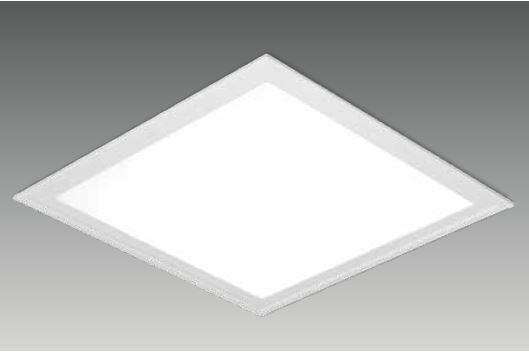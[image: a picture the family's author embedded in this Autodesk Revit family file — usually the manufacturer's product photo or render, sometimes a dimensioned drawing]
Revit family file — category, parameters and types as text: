
# Revit family: G 3030 OPL
name_source: partatom
category: Lighting Fixtures
revit_build: Autodesk Revit 2017 (Build: 20160225_1515(x64)
units: mm (PartAtom-declared; Revit-internal decimal feet)

## family parameters
Always vertical = Yes
Cut with Voids When Loaded = No
Host = Ceiling
Light Source = Yes
OmniClass Number = 23.80.70.11
OmniClass Title = Luminaries for Internal Lighting
Part Type = Normal
Room Calculation Point = No
Round Connector Dimension = Use Diameter
Shared = No

## types (2) — shared parameters
Apparent Load = 10 VA
Color Filter = 16777215
Dimming Lamp Color Temperature Shift = <None>
Emit Shape Visible in Rendering = Yes
Emit from Rectangle Length = 320 mm  [stored 1.04987 ft]
Emit from Rectangle Width = 320 mm  [stored 1.04987 ft]
Light Source Symbol Size = 610 mm
Manufacturer = ARLIGHT
Type Image = G 3030 OPL.JPG
Wattage Comments = 10

## type names (no varying parameters)
- GOPL.3030.10.30
- GOPL.3030.10.40

note: [stored X ft] marks values corroborated as IEEE doubles in the binary element streams (Revit-internal decimal feet)

## geometry (parser evidence)
native form markers: Sweep x1
no freeform markers — native parametric forms only
